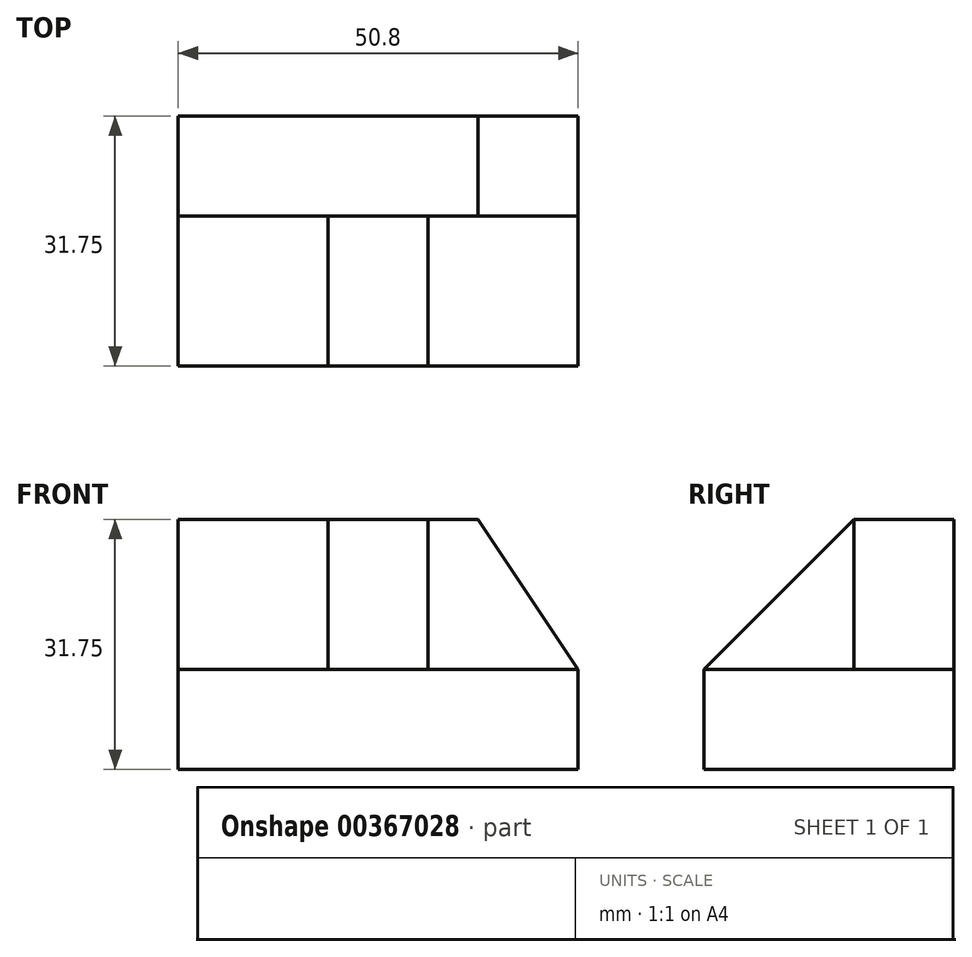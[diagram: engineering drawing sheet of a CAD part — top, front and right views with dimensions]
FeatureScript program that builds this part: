
annotation { "Feature Type Name" : "Feature", "Feature Type Description" : "" }
export const myFeature = defineFeature(function(context is Context, id is Id, definition is map)
    precondition{}
    {
        {
            var Q0;
            Q0=qCreatedBy(makeId("Right.planeOp"),FACE);
            var sketch = newSketch(context, id + "F0", { "sketchPlane" : qUnion([Q0])});
            skLineSegment(sketch, "E0", {"start": v(0, 0) * mm, "end": v(31.75, 0) * mm});
            skLineSegment(sketch, "E1", {"start": v(31.75, 0) * mm, "end": v(31.75, 31.75) * mm});
            skLineSegment(sketch, "E2", {"start": v(31.75, 31.75) * mm, "end": v(0, 31.75) * mm});
            skLineSegment(sketch, "E3", {"start": v(0, 31.75) * mm, "end": v(0, 0) * mm});
            skSolve(sketch);
        }
        {
            var Q0;
            Q0 = qSketchRegion(id + "F0", true);
            extrude(context, id + "F1", {"entities" : qUnion([Q0]), "depth" : 50.8 * mm});
        }
        {
            var Q0;
            Q0=makeQuery(id+"F1.opExtrude","SWEPT_FACE",FACE,{"disambiguationData":[OSD([sQuery(id+"F0.wireOp",EDGE,"E3")])]});
            var sketch = newSketch(context, id + "F2", { "sketchPlane" : qUnion([Q0])});
            skLineSegment(sketch, "E4", {"start": v(38.1, 31.75) * mm, "end": v(50.8, 12.7) * mm});
            skSolve(sketch);
        }
        {
            var Q0;
            Q0 = qSketchRegion(id + "F2", true);
            var Q1;
            {var subQ0=sQuery(id+"F2.wireOp",EDGE,"E4");Q1=makeQuery(id+"F2.imprint","IMPRINT",FACE,{"disambiguationData":[TD([[makeQuery(id+"F2.imprint","IMPRINT",EDGE,{"derivedFrom":subQ0}),1.0]])]});}
            extrude(context, id + "F3", {"entities" : qUnion([Q0, Q1]), "operationType" : NewBodyOperationType.REMOVE, "oppositeDirection" : true, "depth" : 31.75 * mm});
        }
        {
            var Q0;
            Q0=makeQuery(id+"F1.opExtrude","SWEPT_FACE",FACE,{"disambiguationData":[OSD([sQuery(id+"F0.wireOp",EDGE,"E3")])]});
            var sketch = newSketch(context, id + "F4", { "sketchPlane" : qUnion([Q0])});
            skLineSegment(sketch, "E5", {"start": v(50.8, 12.7) * mm, "end": v(31.75, 12.7) * mm});
            skLineSegment(sketch, "E6", {"start": v(31.75, 12.7) * mm, "end": v(31.75, 31.75) * mm});
            skSolve(sketch);
        }
        {
            var Q0;
            Q0 = qSketchRegion(id + "F4", true);
            var Q1;
            Q1=makeQuery(id+"F4.imprint","IMPRINT",FACE,{"disambiguationData":[TD([[makeQuery(id+"F4.imprint","IMPRINT",EDGE,{"derivedFrom":sQuery(id+"F4.wireOp",EDGE,"E5")}),-1.0]])]});
            extrude(context, id + "F5", {"entities" : qUnion([Q0, Q1]), "operationType" : NewBodyOperationType.REMOVE, "oppositeDirection" : true, "depth" : 19.05 * mm});
        }
        {
            var Q0;
            Q0=makeQuery(id+"F5.boolean.opBoolean","COPY",FACE,{"derivedFrom":makeQuery(id+"F5.opExtrude","SWEPT_FACE",FACE,{"disambiguationData":[OSD([sQuery(id+"F4.wireOp",EDGE,"E6")])]})});
            var sketch = newSketch(context, id + "F6", { "sketchPlane" : qUnion([Q0])});
            skLineSegment(sketch, "E7", {"start": v(19.05, 31.75) * mm, "end": v(0, 12.7) * mm});
            skSolve(sketch);
        }
        {
            var Q0;
            Q0 = qSketchRegion(id + "F6", true);
            var Q1;
            Q1=makeQuery(id+"F6.imprint","IMPRINT",FACE,{"disambiguationData":[TD([[makeQuery(id+"F6.imprint","IMPRINT",EDGE,{"derivedFrom":sQuery(id+"F6.wireOp",EDGE,"E7")}),-1.0]])]});
            extrude(context, id + "F7", {"entities" : qUnion([Q0, Q1]), "operationType" : NewBodyOperationType.REMOVE, "oppositeDirection" : true, "depth" : 12.7 * mm});
        }
        {
            var Q0;
            Q0=makeQuery(id+"F1.opExtrude","SWEPT_FACE",FACE,{"disambiguationData":[OSD([sQuery(id+"F0.wireOp",EDGE,"E2")])]});
            var sketch = newSketch(context, id + "F8", { "sketchPlane" : qUnion([Q0])});
            skLineSegment(sketch, "E8", {"start": v(19.05, 19.05) * mm, "end": v(0, 19.05) * mm});
            skSolve(sketch);
        }
        {
            var Q0;
            Q0 = qSketchRegion(id + "F8", true);
            var Q1;
            {var subQ0=sQuery(id+"F8.wireOp",EDGE,"E8");Q1=makeQuery(id+"F8.imprint","IMPRINT",FACE,{"disambiguationData":[TD([[makeQuery(id+"F8.imprint","IMPRINT",EDGE,{"derivedFrom":subQ0}),1.0]])]});}
            extrude(context, id + "F9", {"entities" : qUnion([Q0, Q1]), "operationType" : NewBodyOperationType.REMOVE, "oppositeDirection" : true, "depth" : 19.05 * mm});
        }
    });
